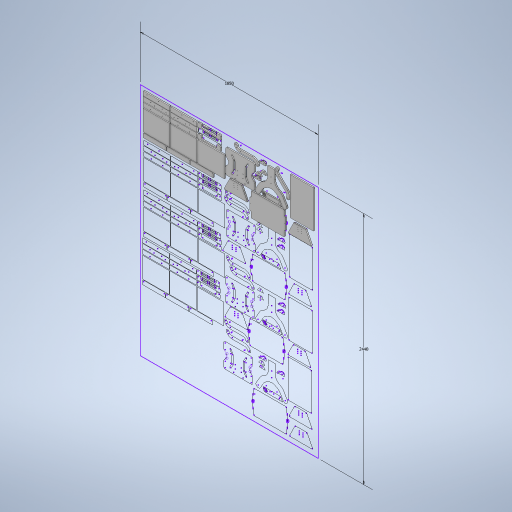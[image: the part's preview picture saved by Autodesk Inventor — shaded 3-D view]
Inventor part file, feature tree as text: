
AUTODESK INVENTOR PART (.ipt)
format: ipt  version: 2024 (Build 280153000, 153)  size: 1,440,256 bytes
history: native  units: mm
features: other x29, extrude x28
ambient origin geometry x8: Origin, YZ Plane, XZ Plane, XY Plane, X Axis, Y Axis, Z Axis, Center Point
bodies: Body1 (feature_tree), Body2 (feature_tree), Body3 (feature_tree), Body4 (feature_tree), Body5 (feature_tree), Body6 (feature_tree), Body7 (feature_tree), Body8 (feature_tree), Body9 (feature_tree), Body10 (feature_tree), Body11 (feature_tree), Body12 (feature_tree), Body13 (feature_tree), Body14 (feature_tree), Body15 (feature_tree), Body16 (feature_tree), Body17 (feature_tree), Body18 (feature_tree), Body19 (feature_tree), Body20 (feature_tree), Body21 (feature_tree), Body22 (feature_tree), Body23 (feature_tree), Body24 (feature_tree), Body25 (feature_tree), Body26 (feature_tree), Body27 (feature_tree), Body28 (feature_tree)
feature tree (57):
  other  "PLACA_SOPORTE_1"
  other  "Visible"
  extrude  "Extrusión1"  Depth=1850.0mm
  extrude  "Extrusión2"  Depth=2440.0mm
  extrude  "Extrusión3"  Depth=12.0mm TaperAngle=0.0deg
  extrude  "Extrusión4"  Depth=12.0mm TaperAngle=0.0deg
  extrude  "Extrusión5"  Depth=12.0mm TaperAngle=0.0deg
  extrude  "Extrusión6"  Depth=12.0mm TaperAngle=0.0deg
  extrude  "Extrusión7"  Depth=12.0mm TaperAngle=0.0deg
  extrude  "Extrusión8"  Depth=12.0mm TaperAngle=0.0deg
  extrude  "Extrusión9"  Depth=12.0mm TaperAngle=0.0deg
  extrude  "Extrusión10"  Depth=12.0mm TaperAngle=0.0deg
  extrude  "Extrusión11"  Depth=12.0mm TaperAngle=0.0deg
  extrude  "Extrusión12"  Depth=12.0mm TaperAngle=0.0deg
  extrude  "Extrusión13"  Depth=12.0mm TaperAngle=0.0deg
  extrude  "Extrusión14"  Depth=12.0mm TaperAngle=0.0deg
  extrude  "Extrusión15"  Depth=12.0mm TaperAngle=0.0deg
  extrude  "Extrusión16"  Depth=12.0mm TaperAngle=0.0deg
  extrude  "Extrusión17"  Depth=12.0mm TaperAngle=0.0deg
  extrude  "Extrusión18"  Depth=12.0mm TaperAngle=0.0deg
  extrude  "Extrusión19"  Depth=12.0mm TaperAngle=0.0deg
  extrude  "Extrusión20"  Depth=12.0mm TaperAngle=0.0deg
  extrude  "Extrusión21"  Depth=12.0mm TaperAngle=0.0deg
  extrude  "Extrusión22"  Depth=12.0mm TaperAngle=0.0deg
  extrude  "Extrusión23"  Depth=12.0mm TaperAngle=0.0deg
  extrude  "Extrusión24"  Depth=12.0mm TaperAngle=0.0deg
  extrude  "Extrusión25"  Depth=12.0mm TaperAngle=0.0deg
  extrude  "Extrusión26"  Depth=12.0mm TaperAngle=0.0deg
  extrude  "Extrusión27"  Depth=12.0mm TaperAngle=0.0deg
  extrude  "Extrusión28"  Depth=12.0mm TaperAngle=0.0deg
  other  "BASE_SOPORTE_1"
  other  "GRADUADOR_INCLINACION_SOPORTE_1"
  other  "SUJECION_CENTRAL_SOPORTE_1"
  other  "SOPORTE_LATERAL_SOPORTE_1"
  other  "SOPORTE_LATERAL_2_SOPORTE_1"
  other  "GRADUADOR_INCLINACION_2_SOPORTE_1"
  other  "BRAZO_SOPORTE_1"
  other  "BRAZO_2_SOPORTE_1"
  other  "PLACA_INFERIOR_MESA_1"
  other  "PLACA_SUPERIOR_MESA_1"
  other  "SOPORTE_LATERAL_I_MESA_1"
  other  "SOPORTE_LATERAL_D_MESA_1"
  other  "BORDE_1"
  other  "BORDE_2"
  other  "BORDE_3"
  other  "BORDE_4"
  other  "BORDE_5"
  other  "BORDE_6"
  other  "PLACA_1"
  other  "PLACA_2"
  other  "PLACA_3"
  other  "POSTERIOR_1"
  other  "POSTERIOR_2"
  other  "POSTERIOR_3"
  other  "FRONTAL_3"
  other  "FRONTAL_1"
  other  "PASADOR_1"
